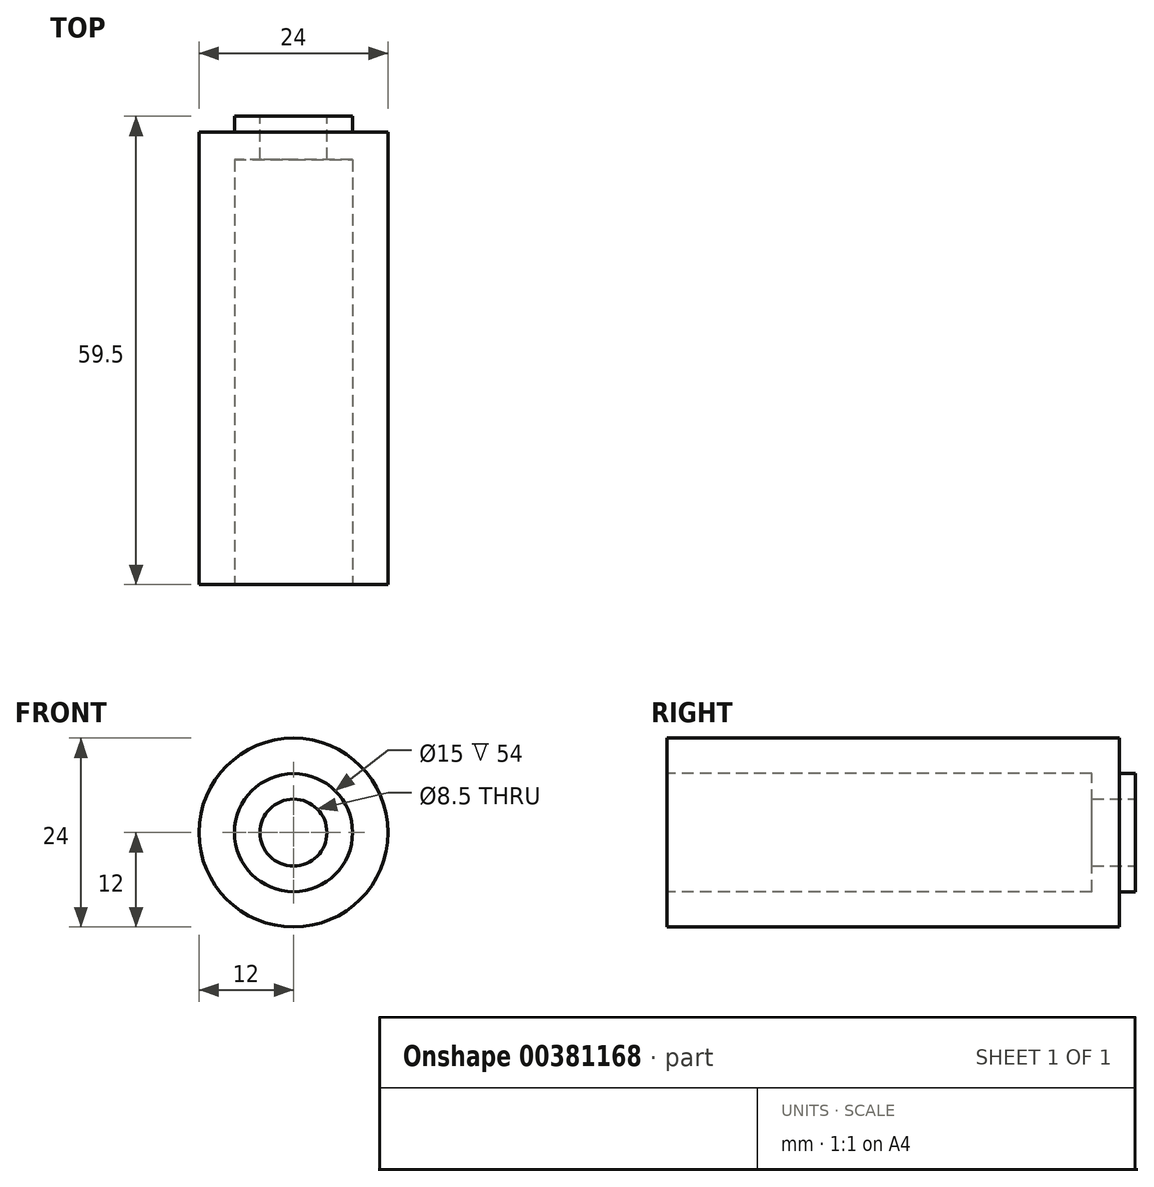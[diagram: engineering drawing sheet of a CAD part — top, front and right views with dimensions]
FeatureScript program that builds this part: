
annotation { "Feature Type Name" : "Feature", "Feature Type Description" : "" }
export const myFeature = defineFeature(function(context is Context, id is Id, definition is map)
    precondition{}
    {
        {
            var Q0;
            Q0=qCreatedBy(makeId("Front.planeOp"),FACE);
            var sketch = newSketch(context, id + "F0", { "sketchPlane" : qUnion([Q0])});
            skCircle(sketch, "E0", {"center": v(0, 0) * mm, "radius": 12 * mm});
            skSolve(sketch);
        }
        {
            var Q0;
            Q0=makeQuery(id+"F0.imprint","IMPRINT",FACE,{"disambiguationData":[TD([[makeQuery(id+"F0.imprint","IMPRINT",EDGE,{"derivedFrom":sQuery(id+"F0.wireOp",EDGE,"E0")}),1.0]])]});
            extrude(context, id + "F1", {"entities" : qUnion([Q0]), "depth" : 57.5 * mm});
        }
        {
            var Q0;
            Q0=makeQuery(id+"F1.opExtrude","CAP_FACE",FACE,{"disambiguationData":[OSD([sQuery(id+"F0.wireOp",EDGE,"E0")])],"isStart":true});
            var sketch = newSketch(context, id + "F2", { "sketchPlane" : qUnion([Q0])});
            skCircle(sketch, "E1", {"center": v(0, 0) * mm, "radius": 7.5 * mm});
            skSolve(sketch);
        }
        {
            var Q0;
            Q0=makeQuery(id+"F2.imprint","IMPRINT",FACE,{"disambiguationData":[TD([[makeQuery(id+"F2.imprint","IMPRINT",EDGE,{"derivedFrom":sQuery(id+"F2.wireOp",EDGE,"E1")}),1.0]])]});
            extrude(context, id + "F3", {"entities" : qUnion([Q0]), "operationType" : NewBodyOperationType.ADD, "depth" : 2 * mm});
        }
        {
            var Q0;
            Q0=makeQuery(id+"F1.opExtrude","CAP_FACE",FACE,{"disambiguationData":[OSD([sQuery(id+"F0.wireOp",EDGE,"E0")])],"isStart":false});
            var sketch = newSketch(context, id + "F4", { "sketchPlane" : qUnion([Q0])});
            skCircle(sketch, "E2", {"center": v(0, 0) * mm, "radius": 7.5 * mm});
            skSolve(sketch);
        }
        {
            var Q0;
            Q0=makeQuery(id+"F4.imprint","IMPRINT",FACE,{"disambiguationData":[TD([[makeQuery(id+"F4.imprint","IMPRINT",EDGE,{"derivedFrom":sQuery(id+"F4.wireOp",EDGE,"E2")}),1.0]])]});
            extrude(context, id + "F5", {"entities" : qUnion([Q0]), "operationType" : NewBodyOperationType.REMOVE, "oppositeDirection" : true, "depth" : 54 * mm});
        }
        {
            var Q0;
            Q0=makeQuery(id+"F3.opExtrude","CAP_FACE",FACE,{"disambiguationData":[OSD([sQuery(id+"F2.wireOp",EDGE,"E1")])],"isStart":false});
            var sketch = newSketch(context, id + "F6", { "sketchPlane" : qUnion([Q0])});
            skCircle(sketch, "E3", {"center": v(0, 0) * mm, "radius": 4.25 * mm});
            skSolve(sketch);
        }
        {
            var Q0;
            Q0=makeQuery(id+"F6.imprint","IMPRINT",FACE,{"disambiguationData":[TD([[makeQuery(id+"F6.imprint","IMPRINT",EDGE,{"derivedFrom":sQuery(id+"F6.wireOp",EDGE,"E3")}),1.0]])]});
            extrude(context, id + "F7", {"entities" : qUnion([Q0]), "operationType" : NewBodyOperationType.REMOVE, "oppositeDirection" : true, "depth" : 8 * mm});
        }
    });
